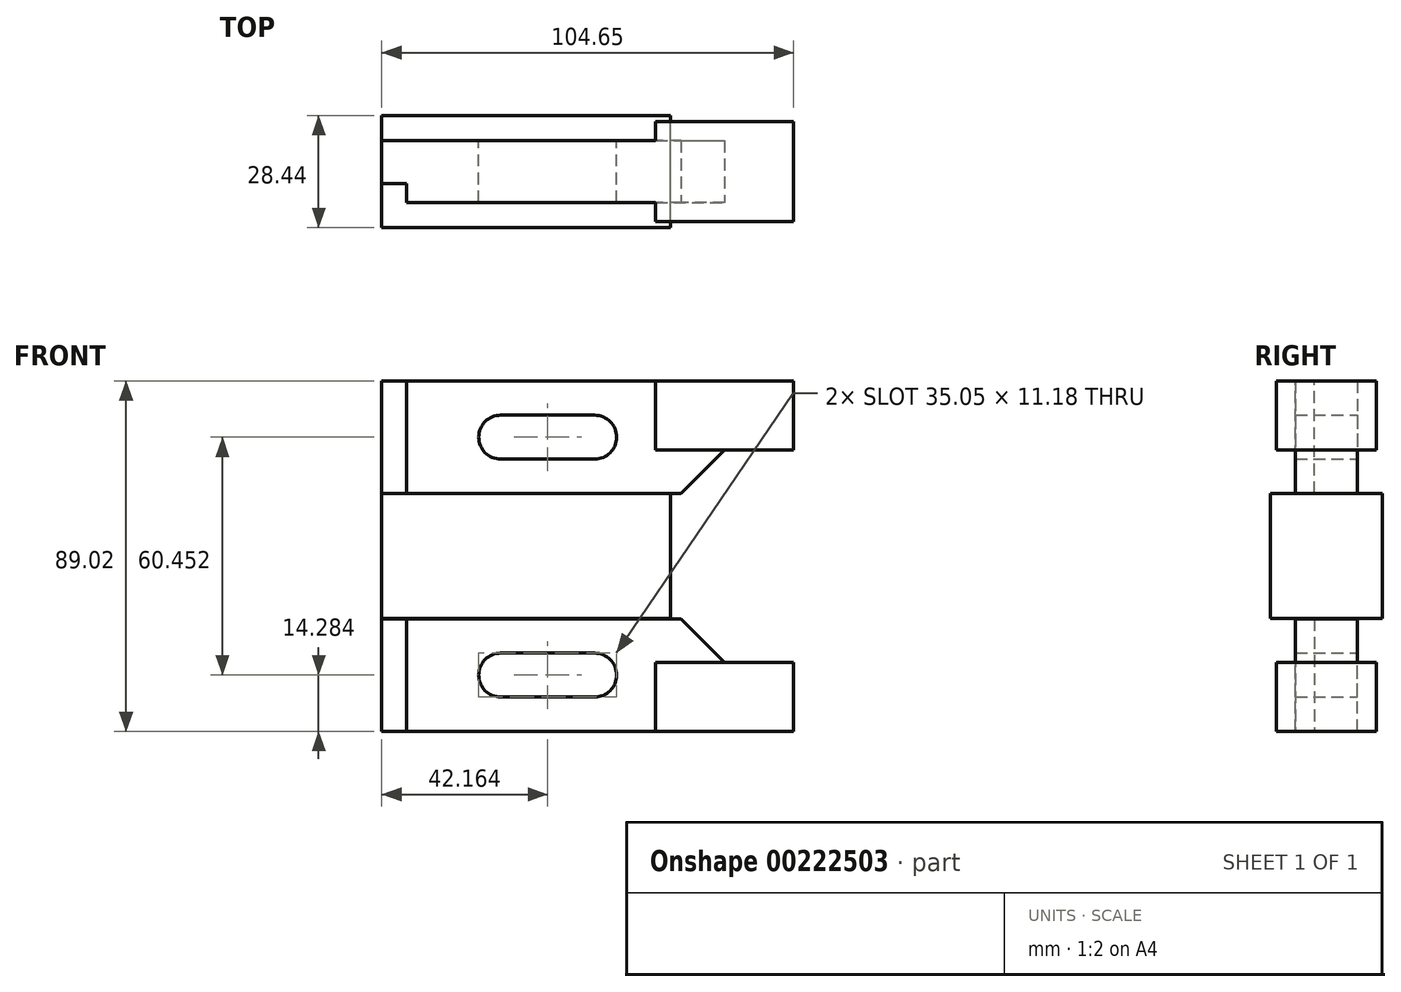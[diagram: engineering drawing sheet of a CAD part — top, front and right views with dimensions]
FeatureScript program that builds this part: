
annotation { "Feature Type Name" : "Feature", "Feature Type Description" : "" }
export const myFeature = defineFeature(function(context is Context, id is Id, definition is map)
    precondition{}
    {
        {
            var Q0;
            Q0=qCreatedBy(makeId("Front.planeOp"),FACE);
            var sketch = newSketch(context, id + "F0", { "sketchPlane" : qUnion([Q0])});
            skLineSegment(sketch, "E0", {"start": v(44.96, 0) * mm, "end": v(44.96, 30.23) * mm, "construction": true});
            skLineSegment(sketch, "E1", {"start": v(44.96, 30.23) * mm, "end": v(-56.89, 30.23) * mm, "construction": true});
            skLineSegment(sketch, "E2", {"start": v(44.96, 0) * mm, "end": v(-61.04, 0) * mm, "construction": true});
            skLineSegment(sketch, "E3", {"start": v(44.96, 30.23) * mm, "end": v(44.96, 44.51) * mm, "construction": true});
            skLineSegment(sketch, "E4", {"start": v(44.96, 44.51) * mm, "end": v(-59.7, 44.51) * mm});
            skLineSegment(sketch, "E5.MirrorCS", {"start": v(44.96, 15.94) * mm, "end": v(-59.7, 15.94) * mm});
            skLineSegment(sketch, "E6", {"start": v(-59.7, 44.51) * mm, "end": v(-59.7, 15.94) * mm});
            skLineSegment(sketch, "E7", {"start": v(44.96, 44.51) * mm, "end": v(44.96, 15.94) * mm});
            skArc(sketch, "E8", {"start": v(-29.46, 35.81) * mm, "mid": v(-35.05, 30.23) * mm, "end": v(-29.46, 24.64) * mm});
            skLineSegment(sketch, "E9", {"start": v(-35.05, 30.23) * mm, "end": v(-35.05, 19.74) * mm, "construction": true});
            skLineSegment(sketch, "E10", {"start": v(-35.05, 19.74) * mm, "end": v(0, 19.74) * mm, "construction": true});
            skLineSegment(sketch, "E11", {"start": v(-17.53, 19.74) * mm, "end": v(-17.53, 41.36) * mm, "construction": true});
            skArc(sketch, "E12.MirrorC", {"start": v(-5.59, 35.81) * mm, "mid": v(0, 30.23) * mm, "end": v(-5.59, 24.64) * mm});
            skLineSegment(sketch, "E13", {"start": v(-29.46, 35.81) * mm, "end": v(-5.59, 35.81) * mm});
            skLineSegment(sketch, "E14.MirrorCS", {"start": v(-29.46, 24.64) * mm, "end": v(-5.59, 24.64) * mm});
            skSolve(sketch);
        }
        {
            var Q0;
            Q0=makeQuery(id+"F0.imprint","IMPRINT",FACE,{"disambiguationData":[TD([[makeQuery(id+"F0.imprint","IMPRINT",EDGE,{"derivedFrom":sQuery(id+"F0.wireOp",EDGE,"E4")}),1.0]])]});
            extrude(context, id + "F1", {"entities" : qUnion([Q0]), "endBound" : BoundingType.SYMMETRIC, "depth" : 25.4 * mm});
        }
        {
            var Q0;
            Q0=makeQuery(id+"F1.opExtrude","SWEPT_FACE",FACE,{"disambiguationData":[OSD([sQuery(id+"F0.wireOp",EDGE,"E4")])]});
            var sketch = newSketch(context, id + "F2", { "sketchPlane" : qUnion([Q0])});
            skLineSegment(sketch, "E15.bottom", {"start": v(-59.7, -12.7) * mm, "end": v(-53.34, -12.7) * mm});
            skLineSegment(sketch, "E15.top", {"start": v(-59.7, -3.05) * mm, "end": v(-53.34, -3.05) * mm});
            skLineSegment(sketch, "E15.left", {"start": v(-59.7, -12.7) * mm, "end": v(-59.7, -3.05) * mm});
            skLineSegment(sketch, "E15.right", {"start": v(-53.34, -12.7) * mm, "end": v(-53.34, -3.05) * mm});
            skSolve(sketch);
        }
        {
            var Q0;
            Q0=makeQuery(id+"F2.imprint","IMPRINT",FACE,{"disambiguationData":[TD([[makeQuery(id+"F2.imprint","IMPRINT",EDGE,{"derivedFrom":sQuery(id+"F2.wireOp",EDGE,"E15.bottom")}),-1.0]])]});
            extrude(context, id + "F3", {"entities" : qUnion([Q0]), "operationType" : NewBodyOperationType.REMOVE, "endBound" : BoundingType.THROUGH_ALL, "oppositeDirection" : true, "depth" : 25.4 * mm});
        }
        {
            var Q0;
            Q0=makeQuery(id+"F1.opExtrude","CAP_FACE",FACE,{"disambiguationData":[OSD([sQuery(id+"F0.wireOp",EDGE,"E4"),sQuery(id+"F0.wireOp",EDGE,"E5.MirrorCS"),sQuery(id+"F0.wireOp",EDGE,"E6"),sQuery(id+"F0.wireOp",EDGE,"E7"),sQuery(id+"F0.wireOp",EDGE,"E8"),sQuery(id+"F0.wireOp",EDGE,"E12.MirrorC"),sQuery(id+"F0.wireOp",EDGE,"E13"),sQuery(id+"F0.wireOp",EDGE,"E14.MirrorCS")])],"isStart":false});
            var sketch = newSketch(context, id + "F4", { "sketchPlane" : qUnion([Q0])});
            skLineSegment(sketch, "E16", {"start": v(-53.34, 44.51) * mm, "end": v(9.9, 44.51) * mm});
            skLineSegment(sketch, "E17", {"start": v(9.9, 44.51) * mm, "end": v(9.9, 26.99) * mm});
            skLineSegment(sketch, "E18", {"start": v(9.9, 26.99) * mm, "end": v(44.96, 26.99) * mm});
            skLineSegment(sketch, "E19", {"start": v(44.96, 26.99) * mm, "end": v(44.96, 15.94) * mm});
            skLineSegment(sketch, "E20", {"start": v(44.96, 15.94) * mm, "end": v(-53.34, 15.94) * mm});
            skLineSegment(sketch, "E21", {"start": v(-53.34, 15.94) * mm, "end": v(-53.34, 44.51) * mm});
            skSolve(sketch);
        }
        {
            var Q0;
            Q0=makeQuery(id+"F4.imprint","IMPRINT",FACE,{"disambiguationData":[TD([[makeQuery(id+"F4.imprint","IMPRINT",EDGE,{"derivedFrom":sQuery(id+"F4.wireOp",EDGE,"E16")}),1.0]])]});
            extrude(context, id + "F5", {"entities" : qUnion([Q0]), "operationType" : NewBodyOperationType.REMOVE, "oppositeDirection" : true, "depth" : 4.83 * mm});
        }
        {
            var Q0;
            Q0=makeQuery(id+"F1.opExtrude","CAP_FACE",FACE,{"disambiguationData":[OSD([sQuery(id+"F0.wireOp",EDGE,"E4"),sQuery(id+"F0.wireOp",EDGE,"E5.MirrorCS"),sQuery(id+"F0.wireOp",EDGE,"E6"),sQuery(id+"F0.wireOp",EDGE,"E7"),sQuery(id+"F0.wireOp",EDGE,"E8"),sQuery(id+"F0.wireOp",EDGE,"E12.MirrorC"),sQuery(id+"F0.wireOp",EDGE,"E13"),sQuery(id+"F0.wireOp",EDGE,"E14.MirrorCS")])],"isStart":true});
            var sketch = newSketch(context, id + "F6", { "sketchPlane" : qUnion([Q0])});
            skLineSegment(sketch, "E22", {"start": v(59.7, 44.51) * mm, "end": v(-9.9, 44.51) * mm});
            skLineSegment(sketch, "E23", {"start": v(-9.9, 44.51) * mm, "end": v(-9.9, 26.99) * mm});
            skLineSegment(sketch, "E24", {"start": v(-9.9, 26.99) * mm, "end": v(-44.96, 26.99) * mm});
            skLineSegment(sketch, "E25", {"start": v(-44.96, 26.99) * mm, "end": v(-44.96, 15.94) * mm});
            skLineSegment(sketch, "E26", {"start": v(-44.96, 15.94) * mm, "end": v(59.7, 15.94) * mm});
            skLineSegment(sketch, "E27", {"start": v(59.7, 15.94) * mm, "end": v(59.7, 44.51) * mm});
            skSolve(sketch);
        }
        {
            var Q0;
            Q0=makeQuery(id+"F6.imprint","IMPRINT",FACE,{"disambiguationData":[TD([[makeQuery(id+"F6.imprint","IMPRINT",EDGE,{"derivedFrom":sQuery(id+"F6.wireOp",EDGE,"E22")}),-1.0]])]});
            extrude(context, id + "F7", {"entities" : qUnion([Q0]), "operationType" : NewBodyOperationType.REMOVE, "oppositeDirection" : true, "depth" : 4.83 * mm});
        }
        {
            var Q0;
            Q0=makeQuery(id+"F1.opExtrude","CAP_FACE",FACE,{"disambiguationData":[OSD([sQuery(id+"F0.wireOp",EDGE,"E4"),sQuery(id+"F0.wireOp",EDGE,"E5.MirrorCS"),sQuery(id+"F0.wireOp",EDGE,"E6"),sQuery(id+"F0.wireOp",EDGE,"E7"),sQuery(id+"F0.wireOp",EDGE,"E8"),sQuery(id+"F0.wireOp",EDGE,"E12.MirrorC"),sQuery(id+"F0.wireOp",EDGE,"E13"),sQuery(id+"F0.wireOp",EDGE,"E14.MirrorCS")])],"isStart":false});
            var sketch = newSketch(context, id + "F8", { "sketchPlane" : qUnion([Q0])});
            skLineSegment(sketch, "E28", {"start": v(44.96, 44.51) * mm, "end": v(16.38, 15.94) * mm});
            skPoint(sketch, "E29.orphan", {"position": v(27.43, 44.51) * mm});
            skLineSegment(sketch, "E30", {"start": v(16.38, 15.94) * mm, "end": v(44.96, 15.94) * mm});
            skLineSegment(sketch, "E31", {"start": v(44.96, 44.51) * mm, "end": v(44.96, 15.94) * mm});
            skSolve(sketch);
        }
        {
            var Q0;
            {var subQ0=sQuery(id+"F8.wireOp",EDGE,"E31");var subQ3=makeQuery(id+"F5.boolean.opBoolean","COPY",EDGE,{"derivedFrom":makeQuery(id+"F5.opExtrude","CAP_EDGE",EDGE,{"disambiguationData":[OSD([sQuery(id+"F4.wireOp",EDGE,"E18")])],"isStart":true})});var subQ5=makeQuery(id+"F8.imprint","INTERSECT",VERTEX,{"derivedFrom":[subQ3,subQ0]});Q0=makeQuery(id+"F8.imprint","IMPRINT",FACE,{"disambiguationData":[TD([[makeQuery(id+"F8.imprint","IMPRINT",EDGE,{"disambiguationData":[TD([[subQ5,1.0]])],"derivedFrom":subQ3}),1.0]])]});}
            var Q1;
            {var subQ0=sQuery(id+"F8.wireOp",EDGE,"E30");Q1=makeQuery(id+"F8.imprint","IMPRINT",FACE,{"disambiguationData":[TD([[makeQuery(id+"F8.imprint","IMPRINT",EDGE,{"derivedFrom":subQ0}),1.0]])]});}
            extrude(context, id + "F9", {"entities" : qUnion([Q0, Q1]), "operationType" : NewBodyOperationType.REMOVE, "endBound" : BoundingType.THROUGH_ALL, "oppositeDirection" : true, "depth" : 25.4 * mm});
        }
        {
            var Q0;
            Q0=qCreatedBy(makeId("Front.planeOp"),FACE);
            var sketch = newSketch(context, id + "F10", { "sketchPlane" : qUnion([Q0])});
            skLineSegment(sketch, "E32", {"start": v(0, -12) * mm, "end": v(-59.7, -12) * mm, "construction": true});
            skLineSegment(sketch, "E33", {"start": v(-59.7, -15.88) * mm, "end": v(-59.7, 15.88) * mm});
            skLineSegment(sketch, "E34", {"start": v(-59.7, 15.88) * mm, "end": v(13.72, 15.88) * mm});
            skLineSegment(sketch, "E35.MirrorCS", {"start": v(-59.7, -15.88) * mm, "end": v(13.72, -15.88) * mm});
            skLineSegment(sketch, "E36", {"start": v(13.72, 15.88) * mm, "end": v(13.72, -15.88) * mm});
            skSolve(sketch);
        }
        {
            var Q0;
            Q0=makeQuery(id+"F10.imprint","IMPRINT",FACE,{"disambiguationData":[TD([[makeQuery(id+"F10.imprint","IMPRINT",EDGE,{"derivedFrom":sQuery(id+"F10.wireOp",EDGE,"E33")}),-1.0]])]});
            extrude(context, id + "F11", {"entities" : qUnion([Q0]), "endBound" : BoundingType.SYMMETRIC, "depth" : 28.45 * mm});
        }
        {
            var Q0;
            Q0=makeQuery(id+"F1.opExtrude","SWEPT_BODY",BODY,{"disambiguationData":[OSD([sQuery(id+"F0.wireOp",EDGE,"E4"),sQuery(id+"F0.wireOp",EDGE,"E5.MirrorCS"),sQuery(id+"F0.wireOp",EDGE,"E6"),sQuery(id+"F0.wireOp",EDGE,"E7"),sQuery(id+"F0.wireOp",EDGE,"E8"),sQuery(id+"F0.wireOp",EDGE,"E12.MirrorC"),sQuery(id+"F0.wireOp",EDGE,"E13"),sQuery(id+"F0.wireOp",EDGE,"E14.MirrorCS")])]});
            var Q1;
            Q1=qCreatedBy(makeId("Top.planeOp"),FACE);
            mirror(context, id + "F12", {"entities" : qUnion([Q0]), "mirrorPlane" : qUnion([Q1])});
        }
    });
